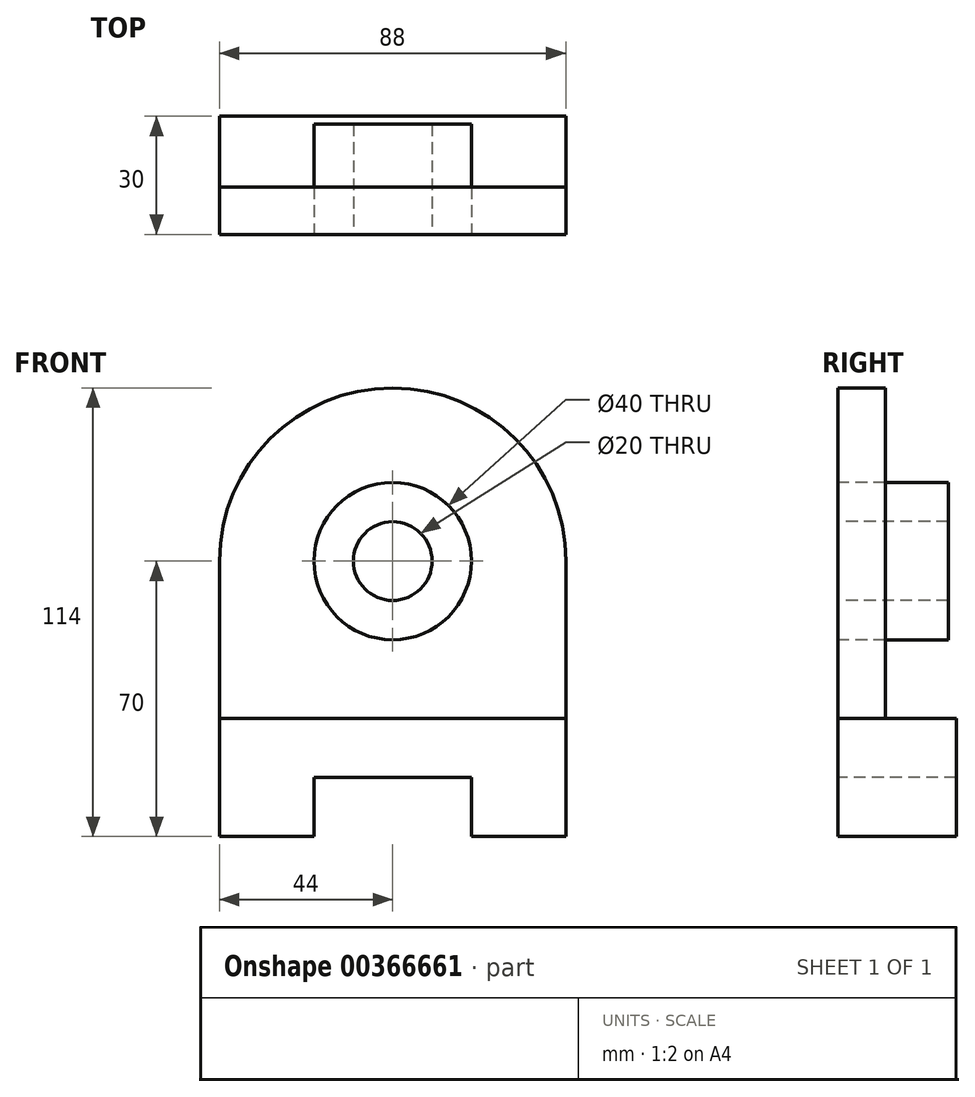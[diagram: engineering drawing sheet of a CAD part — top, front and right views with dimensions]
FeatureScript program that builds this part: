
annotation { "Feature Type Name" : "Feature", "Feature Type Description" : "" }
export const myFeature = defineFeature(function(context is Context, id is Id, definition is map)
    precondition{}
    {
        {
            var Q0;
            Q0=qCreatedBy(makeId("Front.planeOp"),FACE);
            var sketch = newSketch(context, id + "F0", { "sketchPlane" : qUnion([Q0])});
            skLineSegment(sketch, "E0", {"start": v(-44, -30) * mm, "end": v(-20, -30) * mm});
            skLineSegment(sketch, "E1", {"start": v(20, -30) * mm, "end": v(44, -30) * mm});
            skLineSegment(sketch, "E2", {"start": v(-20, -30) * mm, "end": v(-20, -15) * mm});
            skLineSegment(sketch, "E3", {"start": v(-20, -15) * mm, "end": v(20, -15) * mm});
            skLineSegment(sketch, "E4", {"start": v(20, -15) * mm, "end": v(20, -30) * mm});
            skLineSegment(sketch, "E5", {"start": v(44, -30) * mm, "end": v(44, 0) * mm});
            skLineSegment(sketch, "E6", {"start": v(44, 0) * mm, "end": v(-44, 0) * mm});
            skLineSegment(sketch, "E7", {"start": v(-44, 0) * mm, "end": v(-44, -30) * mm});
            skLineSegment(sketch, "E8", {"start": v(-44, 0) * mm, "end": v(-44, 40) * mm});
            skLineSegment(sketch, "E9", {"start": v(44, 0) * mm, "end": v(44, 40) * mm});
            skLineSegment(sketch, "E10", {"start": v(-44, 40) * mm, "end": v(44, 40) * mm, "construction": true});
            skArc(sketch, "E11", {"start": v(44, 40) * mm, "mid": v(0, 84) * mm, "end": v(-44, 40) * mm});
            skCircle(sketch, "E12", {"center": v(0, 40) * mm, "radius": 10 * mm});
            skCircle(sketch, "E13", {"center": v(0, 40) * mm, "radius": 20 * mm});
            skSolve(sketch);
        }
        {
            var Q0;
            Q0=makeQuery(id+"F0.imprint","IMPRINT",FACE,{"disambiguationData":[TD([[makeQuery(id+"F0.imprint","IMPRINT",EDGE,{"derivedFrom":sQuery(id+"F0.wireOp",EDGE,"E0")}),1.0]])]});
            extrude(context, id + "F1", {"entities" : qUnion([Q0]), "oppositeDirection" : true, "depth" : 30 * mm});
        }
        {
            var Q0;
            Q0=makeQuery(id+"F0.imprint","IMPRINT",FACE,{"disambiguationData":[TD([[makeQuery(id+"F0.imprint","IMPRINT",EDGE,{"derivedFrom":sQuery(id+"F0.wireOp",EDGE,"E6")}),-1.0]])]});
            extrude(context, id + "F2", {"entities" : qUnion([Q0]), "oppositeDirection" : true, "depth" : 12 * mm});
        }
        {
            var Q0;
            Q0=makeQuery(id+"F0.imprint","IMPRINT",FACE,{"disambiguationData":[TD([[makeQuery(id+"F0.imprint","IMPRINT",EDGE,{"derivedFrom":sQuery(id+"F0.wireOp",EDGE,"E12")}),-1.0]])]});
            extrude(context, id + "F3", {"entities" : qUnion([Q0]), "oppositeDirection" : true, "depth" : 28 * mm});
        }
    });
